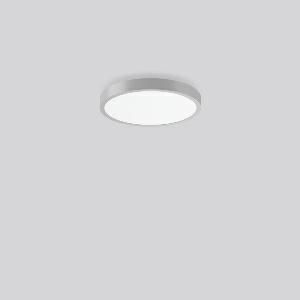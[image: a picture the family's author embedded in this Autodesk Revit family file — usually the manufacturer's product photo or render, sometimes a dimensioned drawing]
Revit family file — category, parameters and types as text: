
# Revit family: triona_round_a_312419_004_1_730_9557
name_source: partatom
category: Lighting Fixtures
units: mm (PartAtom-declared; Revit-internal decimal feet)

## family parameters
Cut with Voids When Loaded = No
Host = Face
Light Source = No
Part Type = Normal
Room Calculation Point = No
Round Connector Dimension = Use Diameter
Shared = No

## types (1)
- TRIONA round A (1 x LED Modul 840, 4900 lm, 4000)
    Apparent Load = 48 VA
    CIE Flux Codes = 49 80 96 100 100
    Color Rendering = 80
    Color Temperature = 4000
    Default Elevation = 1800 mm
    Description = Series: TRIONA round
Decorative round LED surface-mounted luminaire. Flat, seamless frame: aluminium extrusion profile, powder coated. Cover made of sheet steel, powder-coated. Light emission through a diffuser: plastic, opal. Lightguide and diffuser made of non-yellowing plastic (PMMA). Lateral light emission (RZB SIDELITE technology) for above-average homogeneous light distribution. Suitable for Ceiling mounting, Wall (surface). Tool-free mounting via bayonet connection. Electronic ballast included. Very easy installation thanks to Plug+Play connection. With Casambi smart+free Bluetooth control for wireless network and operation using Android / iOS devices, free app available for download. 
Colour: silver, matt (approx. RAL 9006)
Diameter: 461 mm
Height: 88 mm
Lamp: LED
Socket: without socket
Colour temperature: 4000K
Colour rendering index (CRI): 80
System power: 48 W
Rated luminous flux: 4900 lm
Luminous efficiency: 102 lm/W
Control gear: Dimmable Bluetooth converter
Protection class: I
Type of protection: IP 20
    Height = 88 mm
    Lamp = 1 x LED Modul 840
    Lamp Light Flux = 4900 lm
    Lamp count = 1
    Length = 461 mm
    Lifetime = 50000 h
    Luminous efficacy = 102 lm/W
    Manufacturer = RZB
    ModVariant = No
    Model = 312419.004.1.730
    Mounting Place = Ceiling
    Mounting Type = Surface mounted
    Number of Poles = 1
    OnlyDefault = Yes
    Power Factor = 1
    Product Name = TRIONA round A
    Product group = Surface mounted modular luminaires
    ProductGroupID = 306
    Protection Class = Protection class I
    Protection Degree = IP 20
    RLX_Detail_Level = 1
    RLX_Emergency_Light_Flux = 0 lm
    RLX_Emergency_Type = 0
    RLX_Emergency_Type_DB = No
    RlxData = <blob elided: 27869 chars, md5=bd71e03e>
    Socket = socket
    Standby Power = 0 W
    System Light Flux = 4900 lm
    System Power = 48 W
    Type Comments = Product without accessories
    Type Image = 312420.004.jpg
    URL = http://relux.com
    VarID = ---
    Voltage = 230 V
    Voltage Range = 220-240 V
    Weight = 0.00 kg
    Width = 0 mm  [stored 0 ft]

note: [stored X ft] marks values corroborated as IEEE doubles in the binary element streams (Revit-internal decimal feet)

## geometry (parser evidence)
native form markers: Blend x4, Sweep x10
no freeform markers — native parametric forms only
